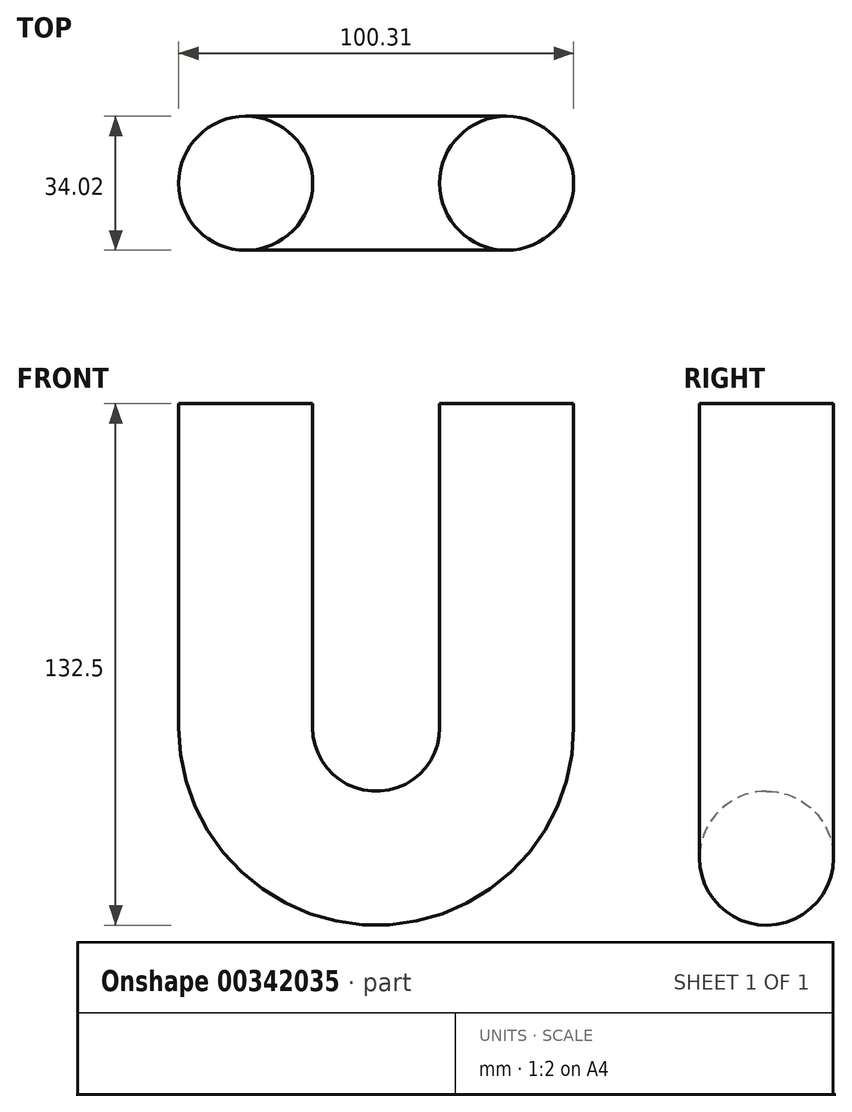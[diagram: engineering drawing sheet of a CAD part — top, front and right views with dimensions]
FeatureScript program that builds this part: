
annotation { "Feature Type Name" : "Feature", "Feature Type Description" : "" }
export const myFeature = defineFeature(function(context is Context, id is Id, definition is map)
    precondition{}
    {
        {
            var Q0;
            Q0=qCreatedBy(makeId("Front.planeOp"),FACE);
            var sketch = newSketch(context, id + "F0", { "sketchPlane" : qUnion([Q0])});
            skLineSegment(sketch, "E0", {"start": v(0, 0) * mm, "end": v(0, -82.34) * mm});
            skArc(sketch, "E1", {"start": v(0, -82.34) * mm, "mid": v(-33.15, -115.48) * mm, "end": v(-66.3, -82.34) * mm});
            skLineSegment(sketch, "E2", {"start": v(-66.3, -82.34) * mm, "end": v(-66.3, 0) * mm});
            skSolve(sketch);
        }
        {
            var Q0;
            Q0=sQuery(id+"F0.wireOp",EDGE,"E2");
            var Q1;
            Q1=sQuery(id+"F0.wireOp",VERTEX,"E2.end");
            cPlane(context, id + "F1", {"entities" : qUnion([Q0, Q1]), "cplaneType" : CPlaneType.CURVE_POINT, "offset" : 25.4 * mm, "width" : 152.4 * mm, "height" : 152.4 * mm});
        }
        {
            var Q0;
            Q0=qCreatedBy(id+"F1.planeOp",FACE);
            var sketch = newSketch(context, id + "F2", { "sketchPlane" : qUnion([Q0])});
            skCircle(sketch, "E3", {"center": v(-66.3, 0) * mm, "radius": 17.01 * mm});
            skSolve(sketch);
        }
        {
            var Q0;
            Q0=makeQuery(id+"F2.imprint","IMPRINT",FACE,{"disambiguationData":[TD([[makeQuery(id+"F2.imprint","IMPRINT",EDGE,{"derivedFrom":sQuery(id+"F2.wireOp",EDGE,"E3")}),1.0]])]});
            var Q1;
            Q1=sQuery(id+"F2.wireOp",EDGE,"E3");
            var Q2;
            Q2 = qBodyType(qCreatedBy(id + "F0" ,EDGE), BodyType.WIRE);
            sweep(context, id + "F3", {"profiles" : qUnion([Q0]), "surfaceProfiles" : qUnion([Q1]), "path" : qUnion([Q2])});
        }
    });
